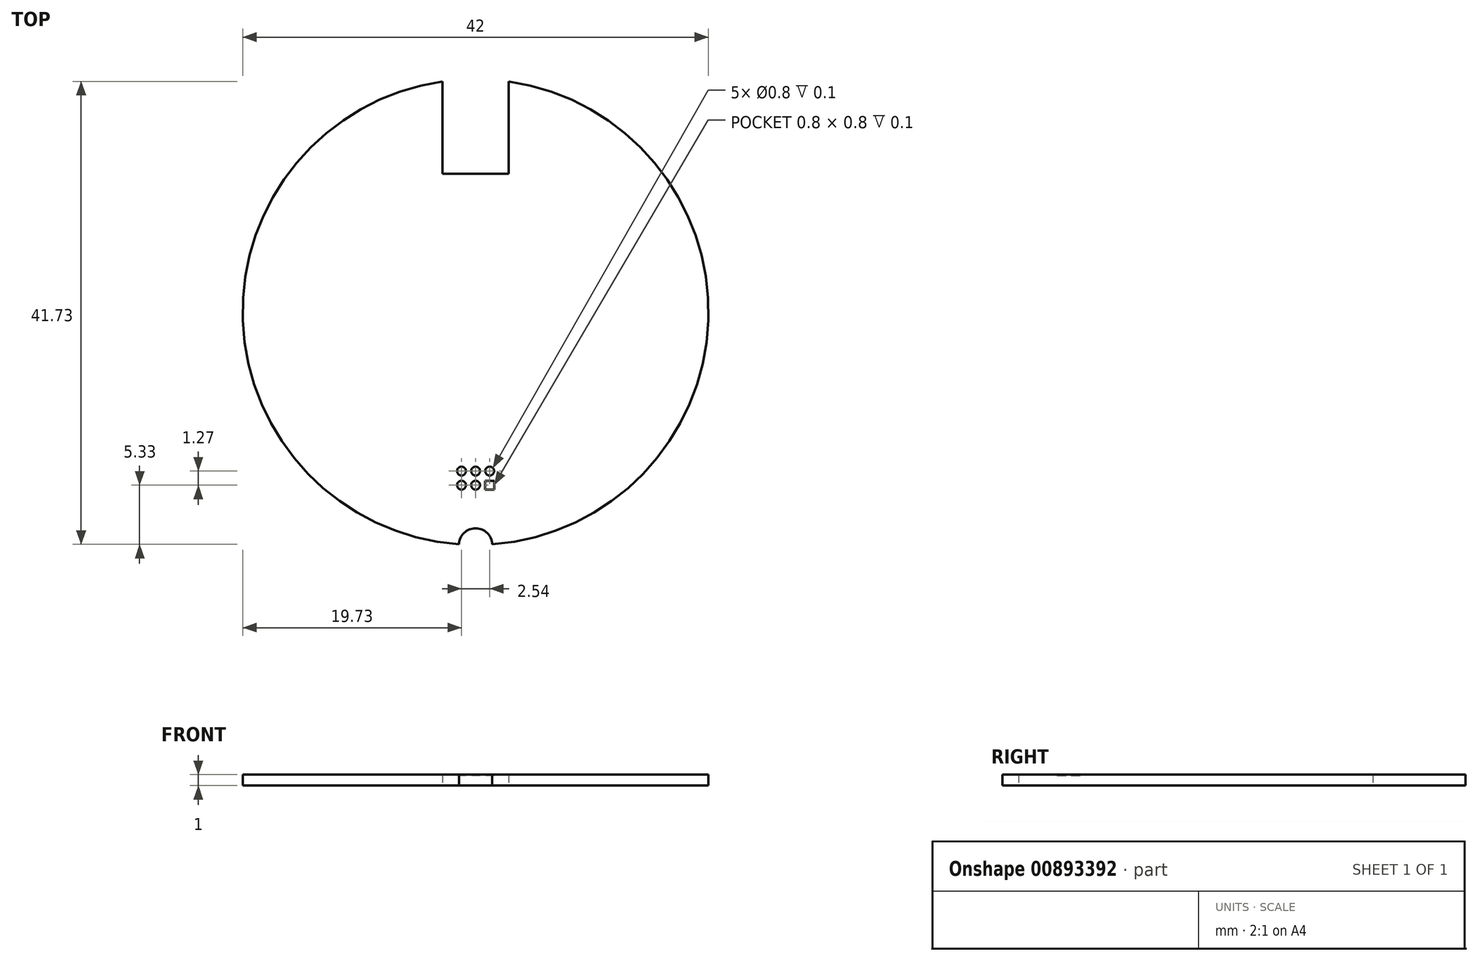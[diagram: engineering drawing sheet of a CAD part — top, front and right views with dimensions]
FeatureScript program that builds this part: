
annotation { "Feature Type Name" : "Feature", "Feature Type Description" : "" }
export const myFeature = defineFeature(function(context is Context, id is Id, definition is map)
    precondition{}
    {
        {
            var Q0;
            Q0=qCreatedBy(makeId("Top.planeOp"),FACE);
            var sketch = newSketch(context, id + "F0", { "sketchPlane" : qUnion([Q0])});
            skArc(sketch, "E0", {"start": v(1.5, -20.95) * mm, "mid": v(20.99, -0.75) * mm, "end": v(3, 20.78) * mm});
            skArc(sketch, "E1", {"start": v(1.5, -20.95) * mm, "mid": v(0, -19.5) * mm, "end": v(-1.5, -20.95) * mm});
            skLineSegment(sketch, "E2.top", {"start": v(-3, 12.45) * mm, "end": v(3, 12.45) * mm});
            skLineSegment(sketch, "E2.left", {"start": v(-3, 20.78) * mm, "end": v(-3, 12.45) * mm});
            skLineSegment(sketch, "E2.right", {"start": v(3, 20.78) * mm, "end": v(3, 12.45) * mm});
            skArc(sketch, "E3.trimOffspring", {"start": v(-3, 20.78) * mm, "mid": v(-20.99, -0.75) * mm, "end": v(-1.5, -20.95) * mm});
            skSolve(sketch);
        }
        {
            var Q0;
            Q0=makeQuery(id+"F0.imprint","IMPRINT",FACE,{"disambiguationData":[TD([[makeQuery(id+"F0.imprint","IMPRINT",EDGE,{"derivedFrom":sQuery(id+"F0.wireOp",EDGE,"E0")}),1.0]])]});
            extrude(context, id + "F1", {"entities" : qUnion([Q0]), "depth" : 1 * mm, "offsetDistance" : 25 * mm});
        }
        {
            var Q0;
            Q0=makeQuery(id+"F1.opExtrude","CAP_FACE",FACE,{"disambiguationData":[OSD([sQuery(id+"F0.wireOp",EDGE,"E0"),sQuery(id+"F0.wireOp",EDGE,"E1")])],"isStart":false});
            var sketch = newSketch(context, id + "F2", { "sketchPlane" : qUnion([Q0])});
            skCircle(sketch, "E4", {"center": v(0, 0) * mm, "radius": 19 * mm});
            skSolve(sketch);
        }
        {
            var Q0;
            Q0=makeQuery(id+"F2.imprint","IMPRINT",FACE,{"disambiguationData":[TD([[makeQuery(id+"F2.imprint","IMPRINT",EDGE,{"derivedFrom":sQuery(id+"F2.wireOp",EDGE,"E4")}),-1.0]])]});
            var sketch = newSketch(context, id + "F3", { "sketchPlane" : qUnion([Q0])});
            skCircle(sketch, "E5", {"center": v(0, -15.62) * mm, "radius": 0.4 * mm});
            skCircle(sketch, "E6", {"center": v(-1.27, -15.62) * mm, "radius": 0.4 * mm});
            skCircle(sketch, "E7", {"center": v(1.27, -14.35) * mm, "radius": 0.4 * mm});
            skCircle(sketch, "E8", {"center": v(0, -14.35) * mm, "radius": 0.4 * mm});
            skCircle(sketch, "E9", {"center": v(-1.27, -14.35) * mm, "radius": 0.4 * mm});
            skLineSegment(sketch, "E10.bottom", {"start": v(1.67, -15.22) * mm, "end": v(0.87, -15.22) * mm});
            skLineSegment(sketch, "E10.top", {"start": v(1.67, -16.02) * mm, "end": v(0.87, -16.02) * mm});
            skLineSegment(sketch, "E10.left", {"start": v(1.67, -15.22) * mm, "end": v(1.67, -16.02) * mm});
            skLineSegment(sketch, "E10.right", {"start": v(0.87, -15.22) * mm, "end": v(0.87, -16.02) * mm});
            skPoint(sketch, "E10.middle", {"position": v(1.27, -15.62) * mm});
            skSolve(sketch);
        }
        {
            var Q0;
            Q0 = qSketchRegion(id + "F3", true);
            extrude(context, id + "F4", {"entities" : qUnion([Q0]), "operationType" : NewBodyOperationType.REMOVE, "oppositeDirection" : true, "depth" : 0.1 * mm, "offsetDistance" : 25 * mm});
        }
    });
